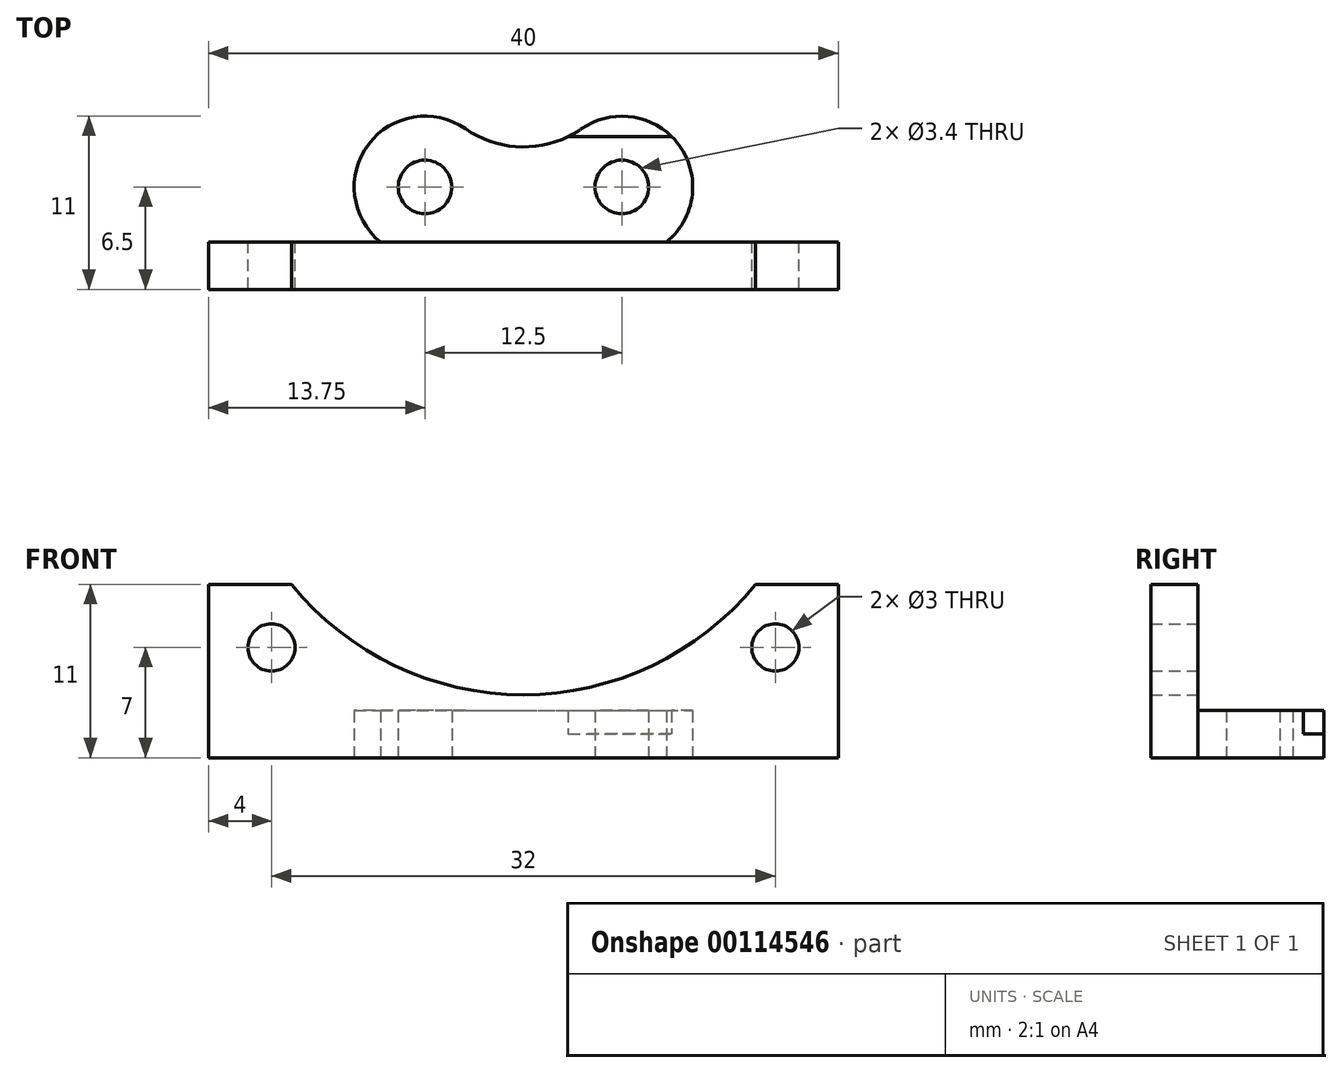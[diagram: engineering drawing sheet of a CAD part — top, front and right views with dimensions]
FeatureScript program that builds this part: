
annotation { "Feature Type Name" : "Feature", "Feature Type Description" : "" }
export const myFeature = defineFeature(function(context is Context, id is Id, definition is map)
    precondition{}
    {
        {
            var Q0;
            Q0=qCreatedBy(makeId("Top.planeOp"),FACE);
            var sketch = newSketch(context, id + "F0", { "sketchPlane" : qUnion([Q0])});
            skLineSegment(sketch, "E0", {"start": v(0, 1.41) * mm, "end": v(0, -1.5) * mm, "construction": true});
            skCircle(sketch, "E1", {"center": v(-6.25, 0) * mm, "radius": 1.7 * mm});
            skCircle(sketch, "E2", {"center": v(6.25, 0) * mm, "radius": 1.7 * mm});
            skArc(sketch, "E3", {"start": v(-3.42, -3.5) * mm, "mid": v(-6.25, 4.5) * mm, "end": v(-9.08, -3.5) * mm});
            skArc(sketch, "E4", {"start": v(9.08, -3.5) * mm, "mid": v(9.85, 2.7) * mm, "end": v(3.68, 3.7) * mm});
            skLineSegment(sketch, "E5", {"start": v(-6.25, 0) * mm, "end": v(6.25, 0) * mm, "construction": true});
            skArc(sketch, "E6", {"start": v(-3.68, 3.7) * mm, "mid": v(0, 2.54) * mm, "end": v(3.68, 3.7) * mm});
            skLineSegment(sketch, "E7", {"start": v(2.84, 3.2) * mm, "end": v(9.41, 3.2) * mm});
            skLineSegment(sketch, "E8", {"start": v(-20, -3.5) * mm, "end": v(20, -3.5) * mm});
            skLineSegment(sketch, "E9", {"start": v(20, -3.5) * mm, "end": v(20, -6.5) * mm});
            skLineSegment(sketch, "E10", {"start": v(20, -6.5) * mm, "end": v(-20, -6.5) * mm});
            skLineSegment(sketch, "E11", {"start": v(-20, -6.5) * mm, "end": v(-20, -3.5) * mm});
            skArc(sketch, "E12.trimOffspring", {"start": v(3.09, 3.2) * mm, "mid": v(1.76, -0.23) * mm, "end": v(3.42, -3.5) * mm});
            skPoint(sketch, "E13", {"position": v(0, -6.5) * mm});
            skPoint(sketch, "E14", {"position": v(0, 2.54) * mm});
            skPoint(sketch, "E15", {"position": v(0, -3.5) * mm});
            skSolve(sketch);
        }
        {
            var Q0;
            {var subQ7=sQuery(id+"F0.wireOp",EDGE,"E9");Q0=makeQuery(id+"F0.imprint","IMPRINT",FACE,{"disambiguationData":[TD([[makeQuery(id+"F0.imprint","IMPRINT",EDGE,{"derivedFrom":subQ7}),-1.0]])]});}
            var Q1;
            Q1=makeQuery(id+"F0.imprint","IMPRINT",FACE,{"disambiguationData":[TD([[makeQuery(id+"F0.imprint","IMPRINT",EDGE,{"derivedFrom":sQuery(id+"F0.wireOp",EDGE,"E1")}),-1.0]])]});
            var Q2;
            {var subQ3=sQuery(id+"F0.wireOp",EDGE,"E12.trimOffspring");Q2=makeQuery(id+"F0.imprint","IMPRINT",FACE,{"disambiguationData":[TD([[makeQuery(id+"F0.imprint","IMPRINT",EDGE,{"derivedFrom":subQ3}),-1.0]])]});}
            var Q3;
            Q3=makeQuery(id+"F0.imprint","IMPRINT",FACE,{"disambiguationData":[TD([[makeQuery(id+"F0.imprint","IMPRINT",EDGE,{"derivedFrom":sQuery(id+"F0.wireOp",EDGE,"E2")}),-1.0]])]});
            var Q4;
            {var subQ0=sQuery(id+"F0.wireOp",EDGE,"E6");var subQ1=sQuery(id+"F0.wireOp",EDGE,"E4");var subQ2=makeQuery(id+"F0.imprint","INTERSECT",VERTEX,{"derivedFrom":[subQ1,subQ0]});Q4=makeQuery(id+"F0.imprint","IMPRINT",FACE,{"disambiguationData":[TD([[makeQuery(id+"F0.imprint","IMPRINT",EDGE,{"disambiguationData":[TD([[subQ2,1.0]])],"derivedFrom":subQ1}),1.0]])]});}
            extrude(context, id + "F1", {"entities" : qUnion([Q0, Q1, Q2, Q3, Q4]), "depth" : 1.5 * mm});
        }
        {
            var Q0;
            Q0=makeQuery(id+"F1.opExtrude","CAP_FACE",FACE,{"disambiguationData":[OSD([sQuery(id+"F0.wireOp",EDGE,"E1"),sQuery(id+"F0.wireOp",EDGE,"E2"),sQuery(id+"F0.wireOp",EDGE,"E3"),sQuery(id+"F0.wireOp",EDGE,"E4"),sQuery(id+"F0.wireOp",EDGE,"E6"),sQuery(id+"F0.wireOp",EDGE,"E8"),sQuery(id+"F0.wireOp",EDGE,"E9"),sQuery(id+"F0.wireOp",EDGE,"E10"),sQuery(id+"F0.wireOp",EDGE,"E11")])],"isStart":false});
            var sketch = newSketch(context, id + "F2", { "sketchPlane" : qUnion([Q0])});
            skCircle(sketch, "E16.1", {"center": v(-6.25, 0) * mm, "radius": 1.7 * mm});
            skCircle(sketch, "E16.2", {"center": v(6.25, 0) * mm, "radius": 1.7 * mm});
            skArc(sketch, "E16.3", {"start": v(-3.42, -3.5) * mm, "mid": v(-6.25, 4.5) * mm, "end": v(-9.08, -3.5) * mm});
            skArc(sketch, "E16.4", {"start": v(9.08, -3.5) * mm, "mid": v(9.85, 2.7) * mm, "end": v(3.68, 3.7) * mm});
            skLineSegment(sketch, "E16.5", {"start": v(-6.25, 0) * mm, "end": v(6.25, 0) * mm, "construction": true});
            skArc(sketch, "E16.6", {"start": v(-3.68, 3.7) * mm, "mid": v(0, 2.54) * mm, "end": v(3.68, 3.7) * mm});
            skLineSegment(sketch, "E16.7", {"start": v(2.84, 3.2) * mm, "end": v(9.41, 3.2) * mm});
            skLineSegment(sketch, "E16.8", {"start": v(-20, -3.5) * mm, "end": v(20, -3.5) * mm});
            skLineSegment(sketch, "E16.9", {"start": v(20, -3.5) * mm, "end": v(20, -6.5) * mm});
            skLineSegment(sketch, "E16.10", {"start": v(20, -6.5) * mm, "end": v(-20, -6.5) * mm});
            skLineSegment(sketch, "E16.11", {"start": v(-20, -6.5) * mm, "end": v(-20, -3.5) * mm});
            skArc(sketch, "E16.12", {"start": v(3.09, 3.2) * mm, "mid": v(1.76, -0.23) * mm, "end": v(3.42, -3.5) * mm});
            skLineSegment(sketch, "E16.13", {"start": v(0, 1.41) * mm, "end": v(0, -1.5) * mm, "construction": true});
            skSolve(sketch);
        }
        {
            var Q0;
            Q0=makeQuery(id+"F2.imprint","IMPRINT",FACE,{"disambiguationData":[TD([[makeQuery(id+"F2.imprint","IMPRINT",EDGE,{"derivedFrom":sQuery(id+"F2.wireOp",EDGE,"E16.1")}),-1.0]])]});
            var Q1;
            {var subQ3=sQuery(id+"F2.wireOp",EDGE,"E16.12");Q1=makeQuery(id+"F2.imprint","IMPRINT",FACE,{"disambiguationData":[TD([[makeQuery(id+"F2.imprint","IMPRINT",EDGE,{"derivedFrom":subQ3}),-1.0]])]});}
            var Q2;
            Q2=makeQuery(id+"F2.imprint","IMPRINT",FACE,{"disambiguationData":[TD([[makeQuery(id+"F2.imprint","IMPRINT",EDGE,{"derivedFrom":sQuery(id+"F2.wireOp",EDGE,"E16.2")}),-1.0]])]});
            var Q3;
            {var subQ7=sQuery(id+"F2.wireOp",EDGE,"E16.9");Q3=makeQuery(id+"F2.imprint","IMPRINT",FACE,{"disambiguationData":[TD([[makeQuery(id+"F2.imprint","IMPRINT",EDGE,{"derivedFrom":subQ7}),-1.0]])]});}
            extrude(context, id + "F3", {"entities" : qUnion([Q0, Q1, Q2, Q3]), "operationType" : NewBodyOperationType.ADD, "depth" : 1.5 * mm});
        }
        {
            var Q0;
            Q0=makeQuery(id+"F3.opExtrude","CAP_FACE",FACE,{"disambiguationData":[OSD([sQuery(id+"F2.wireOp",EDGE,"E16.1"),sQuery(id+"F2.wireOp",EDGE,"E16.2"),sQuery(id+"F2.wireOp",EDGE,"E16.3"),sQuery(id+"F2.wireOp",EDGE,"E16.4"),sQuery(id+"F2.wireOp",EDGE,"E16.6"),sQuery(id+"F2.wireOp",EDGE,"E16.7"),sQuery(id+"F2.wireOp",EDGE,"E16.8"),sQuery(id+"F2.wireOp",EDGE,"E16.9"),sQuery(id+"F2.wireOp",EDGE,"E16.10"),sQuery(id+"F2.wireOp",EDGE,"E16.11")])],"isStart":false});
            var sketch = newSketch(context, id + "F4", { "sketchPlane" : qUnion([Q0])});
            skCircle(sketch, "E17.0", {"center": v(-6.25, 0) * mm, "radius": 1.7 * mm});
            skCircle(sketch, "E17.1", {"center": v(6.25, 0) * mm, "radius": 1.7 * mm});
            skArc(sketch, "E17.2", {"start": v(-3.42, -3.5) * mm, "mid": v(-6.25, 4.5) * mm, "end": v(-9.08, -3.5) * mm});
            skArc(sketch, "E17.3", {"start": v(9.08, -3.5) * mm, "mid": v(9.85, 2.7) * mm, "end": v(3.68, 3.7) * mm});
            skLineSegment(sketch, "E17.4", {"start": v(-6.25, 0) * mm, "end": v(6.25, 0) * mm, "construction": true});
            skArc(sketch, "E17.5", {"start": v(-3.68, 3.7) * mm, "mid": v(0, 2.54) * mm, "end": v(3.68, 3.7) * mm});
            skLineSegment(sketch, "E17.6", {"start": v(2.84, 3.2) * mm, "end": v(9.41, 3.2) * mm});
            skLineSegment(sketch, "E17.7", {"start": v(-20, -3.5) * mm, "end": v(20, -3.5) * mm});
            skLineSegment(sketch, "E17.8", {"start": v(20, -3.5) * mm, "end": v(20, -6.5) * mm});
            skLineSegment(sketch, "E17.9", {"start": v(20, -6.5) * mm, "end": v(-20, -6.5) * mm});
            skLineSegment(sketch, "E17.10", {"start": v(-20, -6.5) * mm, "end": v(-20, -3.5) * mm});
            skArc(sketch, "E17.11", {"start": v(3.09, 3.2) * mm, "mid": v(1.76, -0.23) * mm, "end": v(3.42, -3.5) * mm});
            skLineSegment(sketch, "E17.12", {"start": v(0, 1.41) * mm, "end": v(0, -1.5) * mm, "construction": true});
            skSolve(sketch);
        }
        {
            var Q0;
            {var subQ6=sQuery(id+"F4.wireOp",EDGE,"E17.8");Q0=makeQuery(id+"F4.imprint","IMPRINT",FACE,{"disambiguationData":[TD([[makeQuery(id+"F4.imprint","IMPRINT",EDGE,{"derivedFrom":subQ6}),-1.0]])]});}
            extrude(context, id + "F5", {"entities" : qUnion([Q0]), "operationType" : NewBodyOperationType.ADD, "depth" : 8 * mm});
        }
        {
            var Q0;
            {var subQ0=sQuery(id+"F2.wireOp",EDGE,"E16.8");var subQ1=sQuery(id+"F0.wireOp",EDGE,"E8");Q0=makeQuery(id+"F5.boolean.opBoolean","MERGE",FACE,{"derivedFrom":[makeQuery(id+"F3.boolean.opBoolean","MERGE",FACE,{"derivedFrom":[makeQuery(id+"F1.opExtrude","SWEPT_FACE",FACE,{"disambiguationData":[OSD([subQ1]),TDD([makeQuery(id+"F0.imprint","IMPRINT",EDGE,{"disambiguationData":[TD([[makeQuery(id+"F0.imprint","INTERSECT",VERTEX,{"disambiguationData":[OD(1.0)],"derivedFrom":[sQuery(id+"F0.wireOp",EDGE,"E3"),subQ1]}),1.0]])],"derivedFrom":subQ1})])]}),makeQuery(id+"F3.opExtrude","SWEPT_FACE",FACE,{"disambiguationData":[OSD([subQ0]),TDD([makeQuery(id+"F2.imprint","IMPRINT",EDGE,{"disambiguationData":[TD([[makeQuery(id+"F2.imprint","INTERSECT",VERTEX,{"disambiguationData":[OD(0.0)],"derivedFrom":[sQuery(id+"F2.wireOp",EDGE,"E16.3"),subQ0]}),1.0]])],"derivedFrom":subQ0})])]})]}),makeQuery(id+"F3.boolean.opBoolean","MERGE",FACE,{"derivedFrom":[makeQuery(id+"F1.opExtrude","SWEPT_FACE",FACE,{"disambiguationData":[OSD([subQ1]),TDD([makeQuery(id+"F0.imprint","IMPRINT",EDGE,{"disambiguationData":[TD([[makeQuery(id+"F0.imprint","INTERSECT",VERTEX,{"derivedFrom":[sQuery(id+"F0.wireOp",EDGE,"E4"),subQ1]}),-1.0]])],"derivedFrom":subQ1})])]}),makeQuery(id+"F3.opExtrude","SWEPT_FACE",FACE,{"disambiguationData":[OSD([subQ0]),TDD([makeQuery(id+"F2.imprint","IMPRINT",EDGE,{"disambiguationData":[TD([[makeQuery(id+"F2.imprint","INTERSECT",VERTEX,{"derivedFrom":[sQuery(id+"F2.wireOp",EDGE,"E16.4"),subQ0]}),-1.0]])],"derivedFrom":subQ0})])]})]}),makeQuery(id+"F5.opExtrude","SWEPT_FACE",FACE,{"disambiguationData":[OSD([sQuery(id+"F4.wireOp",EDGE,"E17.7")])]})]});}
            var sketch = newSketch(context, id + "F6", { "sketchPlane" : qUnion([Q0])});
            skLineSegment(sketch, "E18", {"start": v(0, -2.71) * mm, "end": v(0, 14.92) * mm, "construction": true});
            skPoint(sketch, "E18.endSnap0", {"position": v(0, 3) * mm});
            skCircle(sketch, "E19", {"center": v(0, 23) * mm, "radius": 19 * mm});
            skCircle(sketch, "E20", {"center": v(-16, 7) * mm, "radius": 1.5 * mm});
            skCircle(sketch, "E21", {"center": v(16, 7) * mm, "radius": 1.5 * mm});
            skSolve(sketch);
        }
        {
            var Q0;
            Q0=qSketchRegion(id+"F6",true);
            extrude(context, id + "F7", {"entities" : qUnion([Q0]), "operationType" : NewBodyOperationType.REMOVE, "endBound" : BoundingType.THROUGH_ALL, "oppositeDirection" : true, "depth" : 25 * mm});
        }
    });
